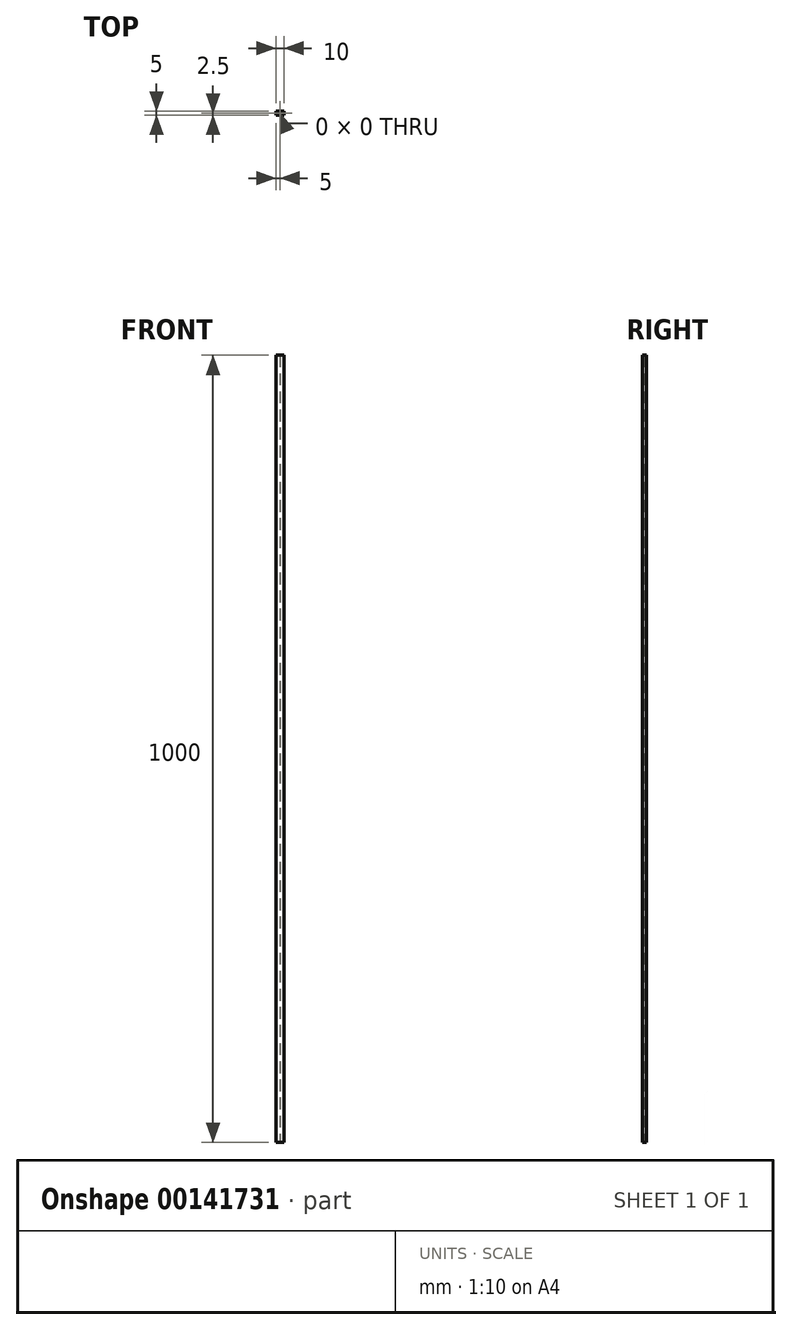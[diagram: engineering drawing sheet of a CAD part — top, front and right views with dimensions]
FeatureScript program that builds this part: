
annotation { "Feature Type Name" : "Feature", "Feature Type Description" : "" }
export const myFeature = defineFeature(function(context is Context, id is Id, definition is map)
    precondition{}
    {
        {
            var Q0;
            Q0=qCreatedBy(makeId("Top.planeOp"),FACE);
            var sketch = newSketch(context, id + "F0", { "sketchPlane" : qUnion([Q0])});
            skLineSegment(sketch, "E0.bottom", {"start": v(0, 0) * mm, "end": v(0, 0) * mm});
            skLineSegment(sketch, "E0.top", {"start": v(0, 0) * mm, "end": v(0, 0) * mm});
            skLineSegment(sketch, "E0.left", {"start": v(0, 0) * mm, "end": v(0, 0) * mm});
            skLineSegment(sketch, "E0.right", {"start": v(0, 0) * mm, "end": v(0, 0) * mm});
            skPoint(sketch, "E0.middle", {"position": v(0, 0) * mm});
            skLineSegment(sketch, "E1.bottom", {"start": v(-5, 2.5) * mm, "end": v(5, 2.5) * mm});
            skLineSegment(sketch, "E1.top", {"start": v(-5, -2.5) * mm, "end": v(5, -2.5) * mm});
            skLineSegment(sketch, "E1.left", {"start": v(-5, 2.5) * mm, "end": v(-5, -2.5) * mm});
            skLineSegment(sketch, "E1.right", {"start": v(5, 2.5) * mm, "end": v(5, -2.5) * mm});
            skSolve(sketch);
        }
        {
            var Q0;
            Q0=makeQuery(id+"F0.imprint","IMPRINT",FACE,{"disambiguationData":[TD([[makeQuery(id+"F0.imprint","IMPRINT",EDGE,{"derivedFrom":sQuery(id+"F0.wireOp",EDGE,"E0.bottom")}),1.0]])]});
            extrude(context, id + "F1", {"entities" : qUnion([Q0]), "depth" : 1000 * mm});
        }
    });
